# Revit family: LIO-Table
name_source: partatom
category: Lighting Fixtures
units: mm (PartAtom-declared; Revit-internal decimal feet)

## family parameters
Always vertical = Yes
Cut with Voids When Loaded = No
Light Source = No
OmniClass Number = 23.80.70.00
OmniClass Title = Lighting
Part Type = Normal
Room Calculation Point = No
Round Connector Dimension = Use Diameter
Shared = No
Work Plane-Based = Yes

## types (3) — shared parameters
Bulb Diametr = 15 mm  [stored 0.0492126 ft]
Default Elevation = 1219 mm
Description = TABLE LAMP
Designer = Studio Debonademeo
Manufacturer = Vistosi
Manufacturer country = Italy
Model = LIO
Type Comments = Studio Debonademeo
URL = https://vistosi.com
URL Product Page = https://vistosi.it
zero-valued in all types: Depth

## per-type parameters (varying)
| type | Height | LIO LT P | LIO Other | Lampshade Type | Width |
| LIO LT P | 230 mm  [stored 0.754593 ft] | Yes | No | LIO_Lampshade : LIO LT P | 7 mm  [stored 0.0229659 ft] |
| LIO LT 40 | 370 mm  [stored 1.21391 ft] | No | Yes | LIO_Lampshade : LIO LT 40 | 14 mm  [stored 0.0459318 ft] |
| LIO LT 50 | 500 mm  [stored 1.64042 ft] | No | Yes | LIO_Lampshade : LIO LT 50 | 18 mm |

note: [stored X ft] marks values corroborated as IEEE doubles in the binary element streams (Revit-internal decimal feet)

## geometry (parser evidence)
native form markers: Sweep x12
no freeform markers — native parametric forms only
